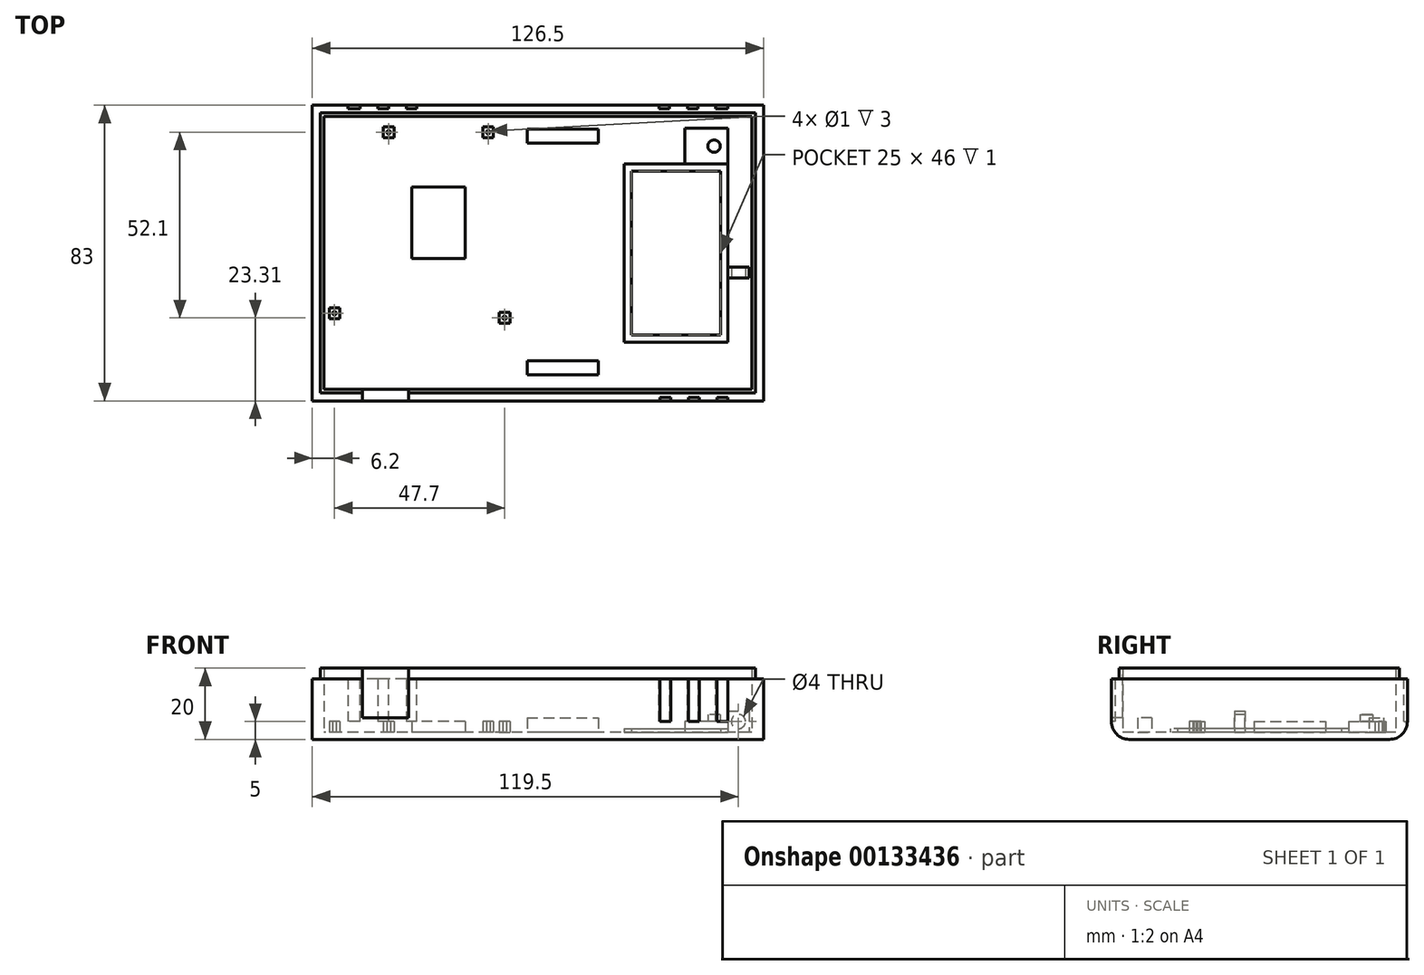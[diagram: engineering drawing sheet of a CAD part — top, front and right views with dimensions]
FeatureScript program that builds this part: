
annotation { "Feature Type Name" : "Feature", "Feature Type Description" : "" }
export const myFeature = defineFeature(function(context is Context, id is Id, definition is map)
    precondition{}
    {
        {
            var Q0;
            Q0=qCreatedBy(makeId("Top.planeOp"),FACE);
            var sketch = newSketch(context, id + "F0", { "sketchPlane" : qUnion([Q0])});
            skLineSegment(sketch, "E0.bottom", {"start": v(63.25, 41.5) * mm, "end": v(-63.25, 41.5) * mm});
            skLineSegment(sketch, "E0.top", {"start": v(63.25, -41.5) * mm, "end": v(-63.25, -41.5) * mm});
            skLineSegment(sketch, "E0.left", {"start": v(63.25, 41.5) * mm, "end": v(63.25, -41.5) * mm});
            skLineSegment(sketch, "E0.right", {"start": v(-63.25, 41.5) * mm, "end": v(-63.25, -41.5) * mm});
            skPoint(sketch, "E0.middle", {"position": v(0, 0) * mm});
            skLineSegment(sketch, "E1.0", {"start": v(-61.25, 39.5) * mm, "end": v(-61.25, -39.5) * mm});
            skLineSegment(sketch, "E1.1", {"start": v(61.25, 39.5) * mm, "end": v(-61.25, 39.5) * mm});
            skLineSegment(sketch, "E1.2", {"start": v(61.25, 39.5) * mm, "end": v(61.25, -39.5) * mm});
            skLineSegment(sketch, "E1.3", {"start": v(61.25, -39.5) * mm, "end": v(-61.25, -39.5) * mm});
            skLineSegment(sketch, "E2", {"start": v(26.25, 23) * mm, "end": v(26.25, -23) * mm});
            skLineSegment(sketch, "E3", {"start": v(26.25, -23) * mm, "end": v(49.25, -23) * mm});
            skLineSegment(sketch, "E4", {"start": v(63.25, 41.5) * mm, "end": v(11.25, 41.5) * mm});
            skLineSegment(sketch, "E5", {"start": v(11.25, 0) * mm, "end": v(-13.75, 0) * mm});
            skLineSegment(sketch, "E6.0", {"start": v(24.25, -25) * mm, "end": v(51.25, -25) * mm});
            skLineSegment(sketch, "E6.1", {"start": v(24.25, 25) * mm, "end": v(24.25, -25) * mm});
            skLineSegment(sketch, "E6.4", {"start": v(51.25, 25) * mm, "end": v(24.25, 25) * mm});
            skLineSegment(sketch, "E7.0", {"start": v(61.05, 39.3) * mm, "end": v(-61.05, 39.3) * mm});
            skLineSegment(sketch, "E7.1", {"start": v(61.05, 39.3) * mm, "end": v(61.05, -39.3) * mm});
            skLineSegment(sketch, "E7.2", {"start": v(61.05, -39.3) * mm, "end": v(-61.05, -39.3) * mm});
            skLineSegment(sketch, "E7.3", {"start": v(-61.05, 39.3) * mm, "end": v(-61.05, -39.3) * mm});
            skLineSegment(sketch, "E8.0", {"start": v(60.05, 38.3) * mm, "end": v(-60.05, 38.3) * mm});
            skLineSegment(sketch, "E8.1", {"start": v(60.05, 38.3) * mm, "end": v(60.05, -38.3) * mm});
            skLineSegment(sketch, "E8.2", {"start": v(60.05, -38.3) * mm, "end": v(-60.05, -38.3) * mm});
            skLineSegment(sketch, "E8.3", {"start": v(-60.05, 38.3) * mm, "end": v(-60.05, -38.3) * mm});
            skLineSegment(sketch, "E9", {"start": v(-63.25, -41.5) * mm, "end": v(-56.25, -41.5) * mm});
            skLineSegment(sketch, "E10", {"start": v(-63.25, -41.5) * mm, "end": v(-43.25, -41.5) * mm});
            skLineSegment(sketch, "E11", {"start": v(-43.25, -41.5) * mm, "end": v(-43.25, -38.3) * mm});
            skLineSegment(sketch, "E12", {"start": v(-56.25, -41.5) * mm, "end": v(-56.25, -38.3) * mm});
            skLineSegment(sketch, "E13", {"start": v(-61.05, -39.3) * mm, "end": v(-2.75, -39.3) * mm});
            skLineSegment(sketch, "E14.right", {"start": v(-4.75, -14.19) * mm, "end": v(-4.75, -18.2) * mm});
            skPoint(sketch, "E14.middle", {"position": v(-4.37, -16.2) * mm});
            skLineSegment(sketch, "E15", {"start": v(-51.75, 34.8) * mm, "end": v(-55.75, 34.8) * mm});
            skLineSegment(sketch, "E16", {"start": v(-3, 34.8) * mm, "end": v(17, 34.8) * mm});
            skLineSegment(sketch, "E17", {"start": v(17, -34.2) * mm, "end": v(-3, -34.2) * mm});
            skLineSegment(sketch, "E18.1", {"start": v(1, 30.8) * mm, "end": v(15, 30.8) * mm});
            skLineSegment(sketch, "E18.2", {"start": v(15, -30.2) * mm, "end": v(1, -30.2) * mm});
            skLineSegment(sketch, "E18.3", {"start": v(1, -18.2) * mm, "end": v(1, -30.2) * mm});
            skLineSegment(sketch, "E19", {"start": v(15, 30.8) * mm, "end": v(17, 30.8) * mm});
            skLineSegment(sketch, "E20", {"start": v(15, -30.2) * mm, "end": v(17, -30.2) * mm});
            skLineSegment(sketch, "E21", {"start": v(17, -34.2) * mm, "end": v(17, -30.2) * mm});
            skLineSegment(sketch, "E22", {"start": v(17, 30.8) * mm, "end": v(17, 34.8) * mm});
            skLineSegment(sketch, "E23", {"start": v(24.25, 25) * mm, "end": v(36.25, 25) * mm});
            skLineSegment(sketch, "E24", {"start": v(53.25, 25) * mm, "end": v(53.25, 35) * mm});
            skLineSegment(sketch, "E25", {"start": v(53.25, 35) * mm, "end": v(41.25, 35) * mm});
            skLineSegment(sketch, "E26", {"start": v(41.25, 35) * mm, "end": v(41.25, 25) * mm});
            skLineSegment(sketch, "E27", {"start": v(53.25, 30) * mm, "end": v(49.42, 30) * mm});
            skPoint(sketch, "E27.endSnap0", {"position": v(36.25, 30) * mm});
            skCircle(sketch, "E28", {"center": v(49.42, 30) * mm, "radius": 1.75 * mm});
            skLineSegment(sketch, "E29", {"start": v(-60.05, -18.2) * mm, "end": v(-57.05, -18.2) * mm});
            skLineSegment(sketch, "E30", {"start": v(-57.05, -18.2) * mm, "end": v(-57.05, -16.9) * mm});
            skLineSegment(sketch, "E31.bottom", {"start": v(-55.55, -18.4) * mm, "end": v(-58.55, -18.4) * mm});
            skLineSegment(sketch, "E31.top", {"start": v(-55.55, -15.4) * mm, "end": v(-58.55, -15.4) * mm});
            skLineSegment(sketch, "E31.left", {"start": v(-55.55, -18.4) * mm, "end": v(-55.55, -15.4) * mm});
            skLineSegment(sketch, "E31.right", {"start": v(-58.55, -18.4) * mm, "end": v(-58.55, -15.4) * mm});
            skPoint(sketch, "E31.middle", {"position": v(-57.05, -16.9) * mm});
            skPoint(sketch, "E32.middle", {"position": v(-4.75, -18.2) * mm});
            skCircle(sketch, "E33", {"center": v(-57.05, -16.9) * mm, "radius": 0.5 * mm});
            skLineSegment(sketch, "E34", {"start": v(-57.05, -16.9) * mm, "end": v(-57.05, 33.9) * mm});
            skLineSegment(sketch, "E35", {"start": v(-57.05, 33.9) * mm, "end": v(-41.85, 33.9) * mm});
            skLineSegment(sketch, "E36", {"start": v(-41.85, 33.9) * mm, "end": v(-13.95, 33.9) * mm});
            skLineSegment(sketch, "E37.bottom", {"start": v(-40.35, 32.4) * mm, "end": v(-43.35, 32.4) * mm});
            skLineSegment(sketch, "E37.top", {"start": v(-40.35, 35.4) * mm, "end": v(-43.35, 35.4) * mm});
            skLineSegment(sketch, "E37.left", {"start": v(-40.35, 32.4) * mm, "end": v(-40.35, 35.4) * mm});
            skLineSegment(sketch, "E37.right", {"start": v(-43.35, 32.4) * mm, "end": v(-43.35, 35.4) * mm});
            skPoint(sketch, "E37.middle", {"position": v(-41.85, 33.9) * mm});
            skLineSegment(sketch, "E38.bottom", {"start": v(-12.45, 32.41) * mm, "end": v(-15.45, 32.41) * mm});
            skLineSegment(sketch, "E38.top", {"start": v(-12.45, 35.41) * mm, "end": v(-15.45, 35.41) * mm});
            skLineSegment(sketch, "E38.left", {"start": v(-12.45, 32.41) * mm, "end": v(-12.45, 35.41) * mm});
            skLineSegment(sketch, "E38.right", {"start": v(-15.45, 32.41) * mm, "end": v(-15.45, 35.41) * mm});
            skPoint(sketch, "E38.middle", {"position": v(-13.95, 33.91) * mm});
            skCircle(sketch, "E39", {"center": v(-41.85, 33.9) * mm, "radius": 0.5 * mm});
            skCircle(sketch, "E40", {"center": v(-13.95, 33.91) * mm, "radius": 0.5 * mm});
            skLineSegment(sketch, "E41", {"start": v(-41.85, 33.9) * mm, "end": v(-27.9, 33.9) * mm});
            skLineSegment(sketch, "E42", {"start": v(-27.9, 33.9) * mm, "end": v(-27.9, -16.9) * mm});
            skLineSegment(sketch, "E43.bottom", {"start": v(-20.4, -1.5) * mm, "end": v(-35.4, -1.5) * mm});
            skLineSegment(sketch, "E43.top", {"start": v(-20.4, 18.5) * mm, "end": v(-35.4, 18.5) * mm});
            skLineSegment(sketch, "E43.left", {"start": v(-20.4, -1.5) * mm, "end": v(-20.4, 18.5) * mm});
            skLineSegment(sketch, "E43.right", {"start": v(-35.4, -1.5) * mm, "end": v(-35.4, 18.5) * mm});
            skPoint(sketch, "E43.middle", {"position": v(-27.9, 8.5) * mm});
            skLineSegment(sketch, "E44", {"start": v(-3, 0) * mm, "end": v(0, 0) * mm});
            skLineSegment(sketch, "E45", {"start": v(0, 0) * mm, "end": v(-3, 0) * mm});
            skLineSegment(sketch, "E46.0", {"start": v(59.25, -4) * mm, "end": v(59.25, -7) * mm});
            skLineSegment(sketch, "E47", {"start": v(57.25, -7) * mm, "end": v(59.25, -7) * mm});
            skLineSegment(sketch, "E48", {"start": v(57.25, -4) * mm, "end": v(59.25, -4) * mm});
            skLineSegment(sketch, "E49", {"start": v(53.25, -7) * mm, "end": v(53.25, -4) * mm});
            skLineSegment(sketch, "E50", {"start": v(53.25, -7) * mm, "end": v(57.25, -7) * mm});
            skLineSegment(sketch, "E51", {"start": v(53.25, -4) * mm, "end": v(57.25, -4) * mm});
            skLineSegment(sketch, "E52", {"start": v(49.25, -23) * mm, "end": v(51.25, -23) * mm});
            skLineSegment(sketch, "E53", {"start": v(51.25, -23) * mm, "end": v(51.25, 23) * mm});
            skLineSegment(sketch, "E54", {"start": v(51.25, -25) * mm, "end": v(53.25, -25) * mm});
            skLineSegment(sketch, "E55", {"start": v(51.25, 25) * mm, "end": v(53.25, 25) * mm});
            skLineSegment(sketch, "E56", {"start": v(53.25, 25) * mm, "end": v(53.25, -25) * mm});
            skLineSegment(sketch, "E57", {"start": v(26.25, 23) * mm, "end": v(51.25, 23) * mm});
            skLineSegment(sketch, "E58", {"start": v(-4.75, -18.2) * mm, "end": v(-4.75, 35.4) * mm});
            skLineSegment(sketch, "E59.bottom", {"start": v(-7.85, -16.7) * mm, "end": v(-10.85, -16.7) * mm});
            skLineSegment(sketch, "E59.top", {"start": v(-7.85, -19.69) * mm, "end": v(-10.85, -19.69) * mm});
            skLineSegment(sketch, "E59.left", {"start": v(-7.85, -16.7) * mm, "end": v(-7.85, -19.69) * mm});
            skLineSegment(sketch, "E59.right", {"start": v(-10.85, -16.7) * mm, "end": v(-10.85, -19.69) * mm});
            skPoint(sketch, "E59.middle", {"position": v(-9.35, -18.19) * mm});
            skCircle(sketch, "E60", {"center": v(-9.35, -18.19) * mm, "radius": 0.5 * mm});
            skLineSegment(sketch, "E61", {"start": v(36.25, 25) * mm, "end": v(24.25, 25) * mm});
            skLineSegment(sketch, "E62", {"start": v(1, 30.8) * mm, "end": v(-3, 30.8) * mm});
            skLineSegment(sketch, "E63", {"start": v(1, -30.2) * mm, "end": v(-3, -30.2) * mm});
            skLineSegment(sketch, "E64", {"start": v(-3, 30.8) * mm, "end": v(-3, 34.8) * mm});
            skLineSegment(sketch, "E65", {"start": v(-3, -30.2) * mm, "end": v(-3, -34.2) * mm});
            skLineSegment(sketch, "E66", {"start": v(-3, -34.2) * mm, "end": v(-3, -30.2) * mm});
            skLineSegment(sketch, "E67", {"start": v(-3, -30.2) * mm, "end": v(17, -30.2) * mm});
            skSolve(sketch);
        }
        {
            var Q0;
            {var subQ8=sQuery(id+"F0.wireOp",EDGE,"E0.bottom");Q0=makeQuery(id+"F0.imprint","IMPRINT",FACE,{"disambiguationData":[TD([[makeQuery(id+"F0.imprint","IMPRINT",EDGE,{"derivedFrom":subQ8}),1.0]])]});}
            var Q1;
            {var subQ4=sQuery(id+"F0.wireOp",EDGE,"E4");Q1=makeQuery(id+"F0.imprint","IMPRINT",FACE,{"disambiguationData":[TD([[makeQuery(id+"F0.imprint","IMPRINT",EDGE,{"derivedFrom":subQ4}),1.0]])]});}
            var Q2;
            Q2=makeQuery(id+"F0.imprint","IMPRINT",FACE,{"disambiguationData":[TD([[makeQuery(id+"F0.imprint","IMPRINT",EDGE,{"derivedFrom":sQuery(id+"F0.wireOp",EDGE,"E1.0")}),1.0]])]});
            var Q3;
            {var subQ8=sQuery(id+"F0.wireOp",EDGE,"E0.top");Q3=makeQuery(id+"F0.imprint","IMPRINT",FACE,{"disambiguationData":[TD([[makeQuery(id+"F0.imprint","IMPRINT",EDGE,{"derivedFrom":subQ8}),-1.0]])]});}
            var Q4;
            {var subQ5=sQuery(id+"F0.wireOp",EDGE,"E1.3");var subQ6=sQuery(id+"F0.wireOp",EDGE,"E1.2");var subQ7=makeQuery(id+"F0.imprint","INTERSECT",VERTEX,{"derivedFrom":[subQ6,subQ5]});Q4=makeQuery(id+"F0.imprint","IMPRINT",FACE,{"disambiguationData":[TD([[makeQuery(id+"F0.imprint","IMPRINT",EDGE,{"disambiguationData":[TD([[subQ7,1.0]])],"derivedFrom":subQ6}),-1.0]])]});}
            var Q5;
            {var subQ0=sQuery(id+"F0.wireOp",EDGE,"E11");var subQ1=sQuery(id+"F0.wireOp",EDGE,"E1.3");var subQ2=makeQuery(id+"F0.imprint","INTERSECT",VERTEX,{"derivedFrom":[subQ1,subQ0]});Q5=makeQuery(id+"F0.imprint","IMPRINT",FACE,{"disambiguationData":[TD([[makeQuery(id+"F0.imprint","IMPRINT",EDGE,{"disambiguationData":[TD([[subQ2,-1.0]])],"derivedFrom":subQ1}),-1.0]])]});}
            var Q6;
            {var subQ0=sQuery(id+"F0.wireOp",EDGE,"E11");var subQ1=sQuery(id+"F0.wireOp",EDGE,"E1.3");var subQ2=makeQuery(id+"F0.imprint","INTERSECT",VERTEX,{"derivedFrom":[subQ1,subQ0]});Q6=makeQuery(id+"F0.imprint","IMPRINT",FACE,{"disambiguationData":[TD([[makeQuery(id+"F0.imprint","IMPRINT",EDGE,{"disambiguationData":[TD([[subQ2,-1.0]])],"derivedFrom":subQ1}),1.0]])]});}
            extrude(context, id + "F1", {"entities" : qUnion([Q0, Q1, Q2, Q3, Q4, Q5, Q6]), "depth" : 17 * mm});
        }
        {
            var Q0;
            Q0=makeQuery(id+"F0.imprint","IMPRINT",FACE,{"disambiguationData":[TD([[makeQuery(id+"F0.imprint","IMPRINT",EDGE,{"derivedFrom":sQuery(id+"F0.wireOp",EDGE,"E6.0")}),-1.0]])]});
            var Q1;
            {var subQ3=sQuery(id+"F0.wireOp",EDGE,"E7.0");Q1=makeQuery(id+"F0.imprint","IMPRINT",FACE,{"disambiguationData":[TD([[makeQuery(id+"F0.imprint","IMPRINT",EDGE,{"derivedFrom":subQ3}),1.0]])]});}
            var Q2;
            Q2=makeQuery(id+"F0.imprint","IMPRINT",FACE,{"disambiguationData":[TD([[makeQuery(id+"F0.imprint","IMPRINT",EDGE,{"derivedFrom":sQuery(id+"F0.wireOp",EDGE,"JjJUV9Ur-tdpk-wXrh-GGUp-oHRZlqTkyCgY")}),1.0]])]});
            var Q3;
            {var subQ0=sQuery(id+"F0.wireOp",EDGE,"QEQ184YT-IDw3-G2xn-FZOk-iXz4uPS1LeEL");Q3=makeQuery(id+"F0.imprint","IMPRINT",FACE,{"disambiguationData":[TD([[makeQuery(id+"F0.imprint","IMPRINT",EDGE,{"derivedFrom":subQ0}),1.0]])]});}
            var Q4;
            {var subQ0=sQuery(id+"F0.wireOp",EDGE,"E11");var subQ1=sQuery(id+"F0.wireOp",EDGE,"E7.2");var subQ2=makeQuery(id+"F0.imprint","INTERSECT",VERTEX,{"derivedFrom":[subQ1,subQ0]});Q4=makeQuery(id+"F0.imprint","IMPRINT",FACE,{"disambiguationData":[TD([[makeQuery(id+"F0.imprint","IMPRINT",EDGE,{"disambiguationData":[TD([[subQ2,-1.0]])],"derivedFrom":subQ1}),-1.0]])]});}
            var Q5;
            {var subQ0=sQuery(id+"F0.wireOp",EDGE,"E11");var subQ1=sQuery(id+"F0.wireOp",EDGE,"E1.3");var subQ2=makeQuery(id+"F0.imprint","INTERSECT",VERTEX,{"derivedFrom":[subQ1,subQ0]});Q5=makeQuery(id+"F0.imprint","IMPRINT",FACE,{"disambiguationData":[TD([[makeQuery(id+"F0.imprint","IMPRINT",EDGE,{"disambiguationData":[TD([[subQ2,-1.0]])],"derivedFrom":subQ1}),-1.0]])]});}
            var Q6;
            {var subQ0=sQuery(id+"F0.wireOp",EDGE,"E11");var subQ1=sQuery(id+"F0.wireOp",EDGE,"E1.3");var subQ2=makeQuery(id+"F0.imprint","INTERSECT",VERTEX,{"derivedFrom":[subQ1,subQ0]});Q6=makeQuery(id+"F0.imprint","IMPRINT",FACE,{"disambiguationData":[TD([[makeQuery(id+"F0.imprint","IMPRINT",EDGE,{"disambiguationData":[TD([[subQ2,-1.0]])],"derivedFrom":subQ1}),1.0]])]});}
            var Q7;
            {var subQ5=sQuery(id+"F0.wireOp",EDGE,"qdQUFwnO-mMan-IZQE-LNTO-aOdIMTajD8fE");Q7=makeQuery(id+"F0.imprint","IMPRINT",FACE,{"disambiguationData":[TD([[makeQuery(id+"F0.imprint","IMPRINT",EDGE,{"derivedFrom":subQ5}),1.0]])]});}
            var Q8;
            Q8=makeQuery(id+"F0.imprint","IMPRINT",FACE,{"disambiguationData":[TD([[makeQuery(id+"F0.imprint","IMPRINT",EDGE,{"derivedFrom":sQuery(id+"F0.wireOp",EDGE,"Yb7JVAUj-9wBk-Ivu1-Xwfn-bJDCMV5gfvpt.right")}),-1.0]])]});
            var Q9;
            {var subQ1=sQuery(id+"F0.wireOp",EDGE,"E14.left");Q9=makeQuery(id+"F0.imprint","IMPRINT",FACE,{"disambiguationData":[TD([[makeQuery(id+"F0.imprint","IMPRINT",EDGE,{"derivedFrom":subQ1}),1.0]])]});}
            var Q10;
            {var subQ4=sQuery(id+"F0.wireOp",EDGE,"E14.bottom");Q10=makeQuery(id+"F0.imprint","IMPRINT",FACE,{"disambiguationData":[TD([[makeQuery(id+"F0.imprint","IMPRINT",EDGE,{"derivedFrom":subQ4}),1.0]])]});}
            var Q11;
            {var subQ3=sQuery(id+"F0.wireOp",EDGE,"Yb7JVAUj-9wBk-Ivu1-Xwfn-bJDCMV5gfvpt.bottom");Q11=makeQuery(id+"F0.imprint","IMPRINT",FACE,{"disambiguationData":[TD([[makeQuery(id+"F0.imprint","IMPRINT",EDGE,{"derivedFrom":subQ3}),1.0]])]});}
            var Q12;
            {var subQ0=sQuery(id+"F0.wireOp",EDGE,"dg6y9XsB-MLs8-b2t9-6rjp-xuShEImU9hPs");var subQ1=sQuery(id+"F0.wireOp",EDGE,"4MlRj56P-oCF8-BNxh-Kgjj-tpuhawxrlBJX");var subQ2=makeQuery(id+"F0.imprint","INTERSECT",VERTEX,{"derivedFrom":[subQ1,subQ0]});Q12=makeQuery(id+"F0.imprint","IMPRINT",FACE,{"disambiguationData":[TD([[makeQuery(id+"F0.imprint","IMPRINT",EDGE,{"disambiguationData":[TD([[subQ2,1.0]])],"derivedFrom":subQ1}),1.0]])]});}
            var Q13;
            {var subQ1=sQuery(id+"F0.wireOp",EDGE,"Yb7JVAUj-9wBk-Ivu1-Xwfn-bJDCMV5gfvpt.top");Q13=makeQuery(id+"F0.imprint","IMPRINT",FACE,{"disambiguationData":[TD([[makeQuery(id+"F0.imprint","IMPRINT",EDGE,{"derivedFrom":subQ1}),1.0]])]});}
            var Q14;
            {var subQ5=sQuery(id+"F0.wireOp",EDGE,"2K8RhCZ3-myJd-tRPz-d2vV-Ilw3Z1lNlUKb");Q14=makeQuery(id+"F0.imprint","IMPRINT",FACE,{"disambiguationData":[TD([[makeQuery(id+"F0.imprint","IMPRINT",EDGE,{"derivedFrom":subQ5}),1.0]])]});}
            var Q15;
            {var subQ0=sQuery(id+"F0.wireOp",EDGE,"E11");var subQ5=sQuery(id+"F0.wireOp",EDGE,"E13");var subQ7=makeQuery(id+"F0.imprint","INTERSECT",VERTEX,{"derivedFrom":[subQ0,subQ5]});Q15=makeQuery(id+"F0.imprint","IMPRINT",FACE,{"disambiguationData":[TD([[makeQuery(id+"F0.imprint","IMPRINT",EDGE,{"disambiguationData":[TD([[subQ7,1.0]])],"derivedFrom":subQ5}),1.0]])]});}
            var Q16;
            Q16=makeQuery(id+"F0.imprint","IMPRINT",FACE,{"disambiguationData":[TD([[makeQuery(id+"F0.imprint","IMPRINT",EDGE,{"derivedFrom":sQuery(id+"F0.wireOp",EDGE,"FxGr0PKn-y8hg-s7OV-rVK9-zofutq62NFjj")}),-1.0]])]});
            var Q17;
            Q17=makeQuery(id+"F0.imprint","IMPRINT",FACE,{"disambiguationData":[TD([[makeQuery(id+"F0.imprint","IMPRINT",EDGE,{"derivedFrom":sQuery(id+"F0.wireOp",EDGE,"M7WSyIMN-nxIa-V6t1-Xdwt-x6DTuTfdMUkq")}),1.0]])]});
            var Q18;
            Q18=makeQuery(id+"F0.imprint","IMPRINT",FACE,{"disambiguationData":[TD([[makeQuery(id+"F0.imprint","IMPRINT",EDGE,{"derivedFrom":sQuery(id+"F0.wireOp",EDGE,"RjNV0yv9-Uhwm-tNHm-vLTt-bpPdpbskBz0X")}),1.0]])]});
            var Q19;
            {var subQ0=sQuery(id+"F0.wireOp",EDGE,"MmGPWXn9-bgj3-SnPU-f73x-K2FSZj5xh2pY");Q19=makeQuery(id+"F0.imprint","IMPRINT",FACE,{"disambiguationData":[TD([[makeQuery(id+"F0.imprint","IMPRINT",EDGE,{"derivedFrom":subQ0}),-1.0]])]});}
            var Q20;
            {var subQ0=sQuery(id+"F0.wireOp",EDGE,"ythX9w36-mhEy-aItk-m4XK-AgucC76ztnV9");Q20=makeQuery(id+"F0.imprint","IMPRINT",FACE,{"disambiguationData":[TD([[makeQuery(id+"F0.imprint","IMPRINT",EDGE,{"derivedFrom":subQ0}),1.0]])]});}
            var Q21;
            {var subQ1=sQuery(id+"F0.wireOp",EDGE,"E16");Q21=makeQuery(id+"F0.imprint","IMPRINT",FACE,{"disambiguationData":[TD([[makeQuery(id+"F0.imprint","IMPRINT",EDGE,{"derivedFrom":subQ1}),-1.0]])]});}
            var Q22;
            {var subQ3=sQuery(id+"F0.wireOp",EDGE,"E23");Q22=makeQuery(id+"F0.imprint","IMPRINT",FACE,{"disambiguationData":[TD([[makeQuery(id+"F0.imprint","IMPRINT",EDGE,{"derivedFrom":subQ3}),1.0]])]});}
            var Q23;
            Q23=makeQuery(id+"F0.imprint","IMPRINT",FACE,{"disambiguationData":[TD([[makeQuery(id+"F0.imprint","IMPRINT",EDGE,{"derivedFrom":sQuery(id+"F0.wireOp",EDGE,"E28")}),1.0]])]});
            var Q24;
            Q24=makeQuery(id+"F0.imprint","IMPRINT",FACE,{"disambiguationData":[TD([[makeQuery(id+"F0.imprint","IMPRINT",EDGE,{"derivedFrom":sQuery(id+"F0.wireOp",EDGE,"Upk9CpIW-mo80-YB5J-z0Jw-Bhem0cwXyb0w")}),1.0]])]});
            var Q25;
            {var subQ0=sQuery(id+"F0.wireOp",EDGE,"E34");var subQ1=sQuery(id+"F0.wireOp",EDGE,"E30");var subQ2=makeQuery(id+"F0.imprint","INTERSECT",VERTEX,{"derivedFrom":[subQ1,subQ0]});Q25=makeQuery(id+"F0.imprint","IMPRINT",FACE,{"disambiguationData":[TD([[makeQuery(id+"F0.imprint","IMPRINT",EDGE,{"disambiguationData":[TD([[subQ2,1.0]])],"derivedFrom":subQ1}),1.0]])]});}
            var Q26;
            {var subQ0=sQuery(id+"F0.wireOp",EDGE,"E34");var subQ1=sQuery(id+"F0.wireOp",EDGE,"E30");var subQ2=makeQuery(id+"F0.imprint","INTERSECT",VERTEX,{"derivedFrom":[subQ1,subQ0]});Q26=makeQuery(id+"F0.imprint","IMPRINT",FACE,{"disambiguationData":[TD([[makeQuery(id+"F0.imprint","IMPRINT",EDGE,{"disambiguationData":[TD([[subQ2,1.0]])],"derivedFrom":subQ1}),-1.0]])]});}
            var Q27;
            Q27=makeQuery(id+"F0.imprint","IMPRINT",FACE,{"disambiguationData":[TD([[makeQuery(id+"F0.imprint","IMPRINT",EDGE,{"derivedFrom":sQuery(id+"F0.wireOp",EDGE,"E40")}),1.0]])]});
            var Q28;
            {var subQ0=sQuery(id+"F0.wireOp",EDGE,"E41");var subQ1=sQuery(id+"F0.wireOp",EDGE,"E35");var subQ2=makeQuery(id+"F0.imprint","INTERSECT",VERTEX,{"derivedFrom":[subQ1,subQ0]});Q28=makeQuery(id+"F0.imprint","IMPRINT",FACE,{"disambiguationData":[TD([[makeQuery(id+"F0.imprint","IMPRINT",EDGE,{"disambiguationData":[TD([[subQ2,1.0]])],"derivedFrom":subQ1}),1.0]])]});}
            var Q29;
            {var subQ0=sQuery(id+"F0.wireOp",EDGE,"E41");var subQ1=sQuery(id+"F0.wireOp",EDGE,"E35");var subQ2=makeQuery(id+"F0.imprint","INTERSECT",VERTEX,{"derivedFrom":[subQ1,subQ0]});Q29=makeQuery(id+"F0.imprint","IMPRINT",FACE,{"disambiguationData":[TD([[makeQuery(id+"F0.imprint","IMPRINT",EDGE,{"disambiguationData":[TD([[subQ2,1.0]])],"derivedFrom":subQ1}),-1.0]])]});}
            var Q30;
            Q30=makeQuery(id+"F0.imprint","IMPRINT",FACE,{"disambiguationData":[TD([[makeQuery(id+"F0.imprint","IMPRINT",EDGE,{"derivedFrom":sQuery(id+"F0.wireOp",EDGE,"E2")}),1.0]])]});
            var Q31;
            Q31=makeQuery(id+"F0.imprint","IMPRINT",FACE,{"disambiguationData":[TD([[makeQuery(id+"F0.imprint","IMPRINT",EDGE,{"derivedFrom":sQuery(id+"F0.wireOp",EDGE,"E46.0")}),-1.0]])]});
            var Q32;
            Q32=makeQuery(id+"F0.imprint","IMPRINT",FACE,{"disambiguationData":[TD([[makeQuery(id+"F0.imprint","IMPRINT",EDGE,{"derivedFrom":sQuery(id+"F0.wireOp",EDGE,"E60")}),1.0]])]});
            var Q33;
            {var subQ3=sQuery(id+"F0.wireOp",EDGE,"E59.bottom");Q33=makeQuery(id+"F0.imprint","IMPRINT",FACE,{"disambiguationData":[TD([[makeQuery(id+"F0.imprint","IMPRINT",EDGE,{"derivedFrom":subQ3}),1.0]])]});}
            var Q34;
            {var subQ0=sQuery(id+"F0.wireOp",EDGE,"E25");Q34=makeQuery(id+"F0.imprint","IMPRINT",FACE,{"disambiguationData":[TD([[makeQuery(id+"F0.imprint","IMPRINT",EDGE,{"derivedFrom":subQ0}),1.0]])]});}
            extrude(context, id + "F2", {"entities" : qUnion([Q0, Q1, Q2, Q3, Q4, Q5, Q6, Q7, Q8, Q9, Q10, Q11, Q12, Q13, Q14, Q15, Q16, Q17, Q18, Q19, Q20, Q21, Q22, Q23, Q24, Q25, Q26, Q27, Q28, Q29, Q30, Q31, Q32, Q33, Q34]), "operationType" : NewBodyOperationType.ADD, "depth" : 2 * mm});
        }
        {
            var Q0;
            Q0=makeQuery(id+"F1.opExtrude","CAP_EDGE",EDGE,{"disambiguationData":[OSD([sQuery(id+"F0.wireOp",EDGE,"E0.bottom"),sQuery(id+"F0.wireOp",EDGE,"E4")])],"isStart":true});
            var Q1;
            Q1=makeQuery(id+"F1.opExtrude","CAP_EDGE",EDGE,{"disambiguationData":[OSD([sQuery(id+"F0.wireOp",EDGE,"E0.top")])],"isStart":true});
            fillet(context, id + "F3", {"entities" : qUnion([Q0, Q1]), "radius" : 5 * mm, "tangentPropagation" : true, "allowEdgeOverflow" : false});
        }
        {
            var Q0;
            Q0=makeQuery(id+"F1.opExtrude","SWEPT_FACE",FACE,{"disambiguationData":[OSD([sQuery(id+"F0.wireOp",EDGE,"E0.bottom"),sQuery(id+"F0.wireOp",EDGE,"E4")])]});
            var sketch = newSketch(context, id + "F4", { "sketchPlane" : qUnion([Q0])});
            skLineSegment(sketch, "E68", {"start": v(-63.25, 17) * mm, "end": v(-0.25, 17) * mm});
            skLineSegment(sketch, "E69", {"start": v(-0.25, 17) * mm, "end": v(-0.25, 3) * mm});
            skLineSegment(sketch, "E70", {"start": v(-63.25, 17) * mm, "end": v(-53.25, 17) * mm});
            skLineSegment(sketch, "E71", {"start": v(-53.25, 17) * mm, "end": v(-53.25, 5) * mm});
            skLineSegment(sketch, "E72", {"start": v(-53.25, 5) * mm, "end": v(-49.9, 5) * mm});
            skLineSegment(sketch, "E73", {"start": v(-49.9, 5) * mm, "end": v(-49.9, 17) * mm});
            skLineSegment(sketch, "E74", {"start": v(-49.9, 17) * mm, "end": v(-44.9, 17) * mm});
            skLineSegment(sketch, "E75", {"start": v(-44.9, 17) * mm, "end": v(-44.9, 5) * mm});
            skLineSegment(sketch, "E76", {"start": v(-44.9, 5) * mm, "end": v(-41.9, 5) * mm});
            skLineSegment(sketch, "E77", {"start": v(-41.9, 5) * mm, "end": v(-41.9, 17) * mm});
            skLineSegment(sketch, "E78", {"start": v(-41.9, 17) * mm, "end": v(-36.9, 17) * mm});
            skLineSegment(sketch, "E79", {"start": v(-36.9, 17) * mm, "end": v(-36.9, 5) * mm});
            skLineSegment(sketch, "E80", {"start": v(-36.9, 5) * mm, "end": v(-33.9, 5) * mm});
            skLineSegment(sketch, "E81", {"start": v(-33.9, 5) * mm, "end": v(-33.9, 17) * mm});
            skLineSegment(sketch, "E82.MirrorCS", {"start": v(33.9, 5) * mm, "end": v(33.9, 17) * mm});
            skLineSegment(sketch, "E83.MirrorCS", {"start": v(36.9, 17) * mm, "end": v(36.9, 5) * mm});
            skLineSegment(sketch, "E84.MirrorCS", {"start": v(41.9, 5) * mm, "end": v(41.9, 17) * mm});
            skLineSegment(sketch, "E85.MirrorCS", {"start": v(44.9, 17) * mm, "end": v(44.9, 5) * mm});
            skLineSegment(sketch, "E86.MirrorCS", {"start": v(49.9, 5) * mm, "end": v(49.9, 17) * mm});
            skLineSegment(sketch, "E87.MirrorCS", {"start": v(53.25, 17) * mm, "end": v(53.25, 5) * mm});
            skLineSegment(sketch, "E88.MirrorCS", {"start": v(36.9, 5) * mm, "end": v(33.9, 5) * mm});
            skLineSegment(sketch, "E89.MirrorCS", {"start": v(44.9, 5) * mm, "end": v(41.9, 5) * mm});
            skLineSegment(sketch, "E90.MirrorCS", {"start": v(63.25, 17) * mm, "end": v(0.25, 17) * mm});
            skLineSegment(sketch, "E91.MirrorCS", {"start": v(53.25, 5) * mm, "end": v(49.9, 5) * mm});
            skLineSegment(sketch, "E92", {"start": v(33.9, 17) * mm, "end": v(36.9, 17) * mm});
            skLineSegment(sketch, "E93", {"start": v(41.9, 17) * mm, "end": v(44.9, 17) * mm});
            skLineSegment(sketch, "E94", {"start": v(49.9, 17) * mm, "end": v(53.25, 17) * mm});
            skSolve(sketch);
        }
        {
            var Q0;
            Q0=makeQuery(id+"F0.imprint","IMPRINT",FACE,{"disambiguationData":[TD([[makeQuery(id+"F0.imprint","IMPRINT",EDGE,{"derivedFrom":sQuery(id+"F0.wireOp",EDGE,"JjJUV9Ur-tdpk-wXrh-GGUp-oHRZlqTkyCgY")}),-1.0]])]});
            var Q1;
            Q1=makeQuery(id+"F0.imprint","IMPRINT",FACE,{"disambiguationData":[TD([[makeQuery(id+"F0.imprint","IMPRINT",EDGE,{"derivedFrom":sQuery(id+"F0.wireOp",EDGE,"E2")}),-1.0]])]});
            extrude(context, id + "F5", {"entities" : qUnion([Q0, Q1]), "operationType" : NewBodyOperationType.ADD, "depth" : 3 * mm});
        }
        {
            var Q0;
            {var subQ3=sQuery(id+"F0.wireOp",EDGE,"E7.0");Q0=makeQuery(id+"F0.imprint","IMPRINT",FACE,{"disambiguationData":[TD([[makeQuery(id+"F0.imprint","IMPRINT",EDGE,{"derivedFrom":subQ3}),1.0]])]});}
            var Q1;
            {var subQ0=sQuery(id+"F0.wireOp",EDGE,"E11");var subQ1=sQuery(id+"F0.wireOp",EDGE,"E8.2");var subQ2=makeQuery(id+"F0.imprint","INTERSECT",VERTEX,{"derivedFrom":[subQ1,subQ0]});Q1=makeQuery(id+"F0.imprint","IMPRINT",FACE,{"disambiguationData":[TD([[makeQuery(id+"F0.imprint","IMPRINT",EDGE,{"disambiguationData":[TD([[subQ2,-1.0]])],"derivedFrom":subQ1}),1.0]])]});}
            extrude(context, id + "F6", {"entities" : qUnion([Q0, Q1]), "operationType" : NewBodyOperationType.ADD, "depth" : 20 * mm, "hasSecondDirection" : true, "secondDirectionOppositeDirection" : false, "secondDirectionDepth" : 2 * mm});
        }
        {
            var Q0;
            {var subQ5=sQuery(id+"F0.wireOp",EDGE,"qdQUFwnO-mMan-IZQE-LNTO-aOdIMTajD8fE");Q0=makeQuery(id+"F0.imprint","IMPRINT",FACE,{"disambiguationData":[TD([[makeQuery(id+"F0.imprint","IMPRINT",EDGE,{"derivedFrom":subQ5}),1.0]])]});}
            var Q1;
            {var subQ4=sQuery(id+"F0.wireOp",EDGE,"E14.left");Q1=makeQuery(id+"F0.imprint","IMPRINT",FACE,{"disambiguationData":[TD([[makeQuery(id+"F0.imprint","IMPRINT",EDGE,{"derivedFrom":subQ4}),1.0]])]});}
            var Q2;
            Q2=makeQuery(id+"F0.imprint","IMPRINT",FACE,{"disambiguationData":[TD([[makeQuery(id+"F0.imprint","IMPRINT",EDGE,{"derivedFrom":sQuery(id+"F0.wireOp",EDGE,"Yb7JVAUj-9wBk-Ivu1-Xwfn-bJDCMV5gfvpt.right")}),-1.0]])]});
            var Q3;
            {var subQ3=sQuery(id+"F0.wireOp",EDGE,"Yb7JVAUj-9wBk-Ivu1-Xwfn-bJDCMV5gfvpt.bottom");Q3=makeQuery(id+"F0.imprint","IMPRINT",FACE,{"disambiguationData":[TD([[makeQuery(id+"F0.imprint","IMPRINT",EDGE,{"derivedFrom":subQ3}),1.0]])]});}
            var Q4;
            {var subQ1=sQuery(id+"F0.wireOp",EDGE,"E14.bottom");Q4=makeQuery(id+"F0.imprint","IMPRINT",FACE,{"disambiguationData":[TD([[makeQuery(id+"F0.imprint","IMPRINT",EDGE,{"derivedFrom":subQ1}),1.0]])]});}
            var Q5;
            {var subQ5=sQuery(id+"F0.wireOp",EDGE,"2K8RhCZ3-myJd-tRPz-d2vV-Ilw3Z1lNlUKb");Q5=makeQuery(id+"F0.imprint","IMPRINT",FACE,{"disambiguationData":[TD([[makeQuery(id+"F0.imprint","IMPRINT",EDGE,{"derivedFrom":subQ5}),1.0]])]});}
            var Q6;
            Q6=makeQuery(id+"F0.imprint","IMPRINT",FACE,{"disambiguationData":[TD([[makeQuery(id+"F0.imprint","IMPRINT",EDGE,{"derivedFrom":sQuery(id+"F0.wireOp",EDGE,"FxGr0PKn-y8hg-s7OV-rVK9-zofutq62NFjj")}),-1.0]])]});
            var Q7;
            {var subQ3=sQuery(id+"F0.wireOp",EDGE,"E23");Q7=makeQuery(id+"F0.imprint","IMPRINT",FACE,{"disambiguationData":[TD([[makeQuery(id+"F0.imprint","IMPRINT",EDGE,{"derivedFrom":subQ3}),1.0]])]});}
            var Q8;
            Q8=makeQuery(id+"F0.imprint","IMPRINT",FACE,{"disambiguationData":[TD([[makeQuery(id+"F0.imprint","IMPRINT",EDGE,{"derivedFrom":sQuery(id+"F0.wireOp",EDGE,"E28")}),1.0]])]});
            var Q9;
            {var subQ5=sQuery(id+"F0.wireOp",EDGE,"E43.left");Q9=makeQuery(id+"F0.imprint","IMPRINT",FACE,{"disambiguationData":[TD([[makeQuery(id+"F0.imprint","IMPRINT",EDGE,{"derivedFrom":subQ5}),1.0]])]});}
            var Q10;
            {var subQ5=sQuery(id+"F0.wireOp",EDGE,"E43.right");Q10=makeQuery(id+"F0.imprint","IMPRINT",FACE,{"disambiguationData":[TD([[makeQuery(id+"F0.imprint","IMPRINT",EDGE,{"derivedFrom":subQ5}),-1.0]])]});}
            var Q11;
            {var subQ1=sQuery(id+"F0.wireOp",EDGE,"E38.bottom");Q11=makeQuery(id+"F0.imprint","IMPRINT",FACE,{"disambiguationData":[TD([[makeQuery(id+"F0.imprint","IMPRINT",EDGE,{"derivedFrom":subQ1}),-1.0]])]});}
            var Q12;
            {var subQ1=sQuery(id+"F0.wireOp",EDGE,"E37.top");Q12=makeQuery(id+"F0.imprint","IMPRINT",FACE,{"disambiguationData":[TD([[makeQuery(id+"F0.imprint","IMPRINT",EDGE,{"derivedFrom":subQ1}),1.0]])]});}
            var Q13;
            {var subQ1=sQuery(id+"F0.wireOp",EDGE,"E37.bottom");Q13=makeQuery(id+"F0.imprint","IMPRINT",FACE,{"disambiguationData":[TD([[makeQuery(id+"F0.imprint","IMPRINT",EDGE,{"derivedFrom":subQ1}),-1.0]])]});}
            var Q14;
            Q14=makeQuery(id+"F0.imprint","IMPRINT",FACE,{"disambiguationData":[TD([[makeQuery(id+"F0.imprint","IMPRINT",EDGE,{"derivedFrom":sQuery(id+"F0.wireOp",EDGE,"E32.bottom")}),1.0]])]});
            var Q15;
            {var subQ4=sQuery(id+"F0.wireOp",EDGE,"E31.bottom");Q15=makeQuery(id+"F0.imprint","IMPRINT",FACE,{"disambiguationData":[TD([[makeQuery(id+"F0.imprint","IMPRINT",EDGE,{"derivedFrom":subQ4}),-1.0]])]});}
            var Q16;
            {var subQ3=sQuery(id+"F0.wireOp",EDGE,"E29");var subQ5=sQuery(id+"F0.wireOp",EDGE,"E30");var subQ6=makeQuery(id+"F0.imprint","INTERSECT",VERTEX,{"derivedFrom":[subQ3,subQ5]});Q16=makeQuery(id+"F0.imprint","IMPRINT",FACE,{"disambiguationData":[TD([[makeQuery(id+"F0.imprint","IMPRINT",EDGE,{"disambiguationData":[TD([[subQ6,1.0]])],"derivedFrom":subQ3}),1.0]])]});}
            var Q17;
            {var subQ3=sQuery(id+"F0.wireOp",EDGE,"E59.bottom");Q17=makeQuery(id+"F0.imprint","IMPRINT",FACE,{"disambiguationData":[TD([[makeQuery(id+"F0.imprint","IMPRINT",EDGE,{"derivedFrom":subQ3}),1.0]])]});}
            var Q18;
            {var subQ0=sQuery(id+"F0.wireOp",EDGE,"E25");Q18=makeQuery(id+"F0.imprint","IMPRINT",FACE,{"disambiguationData":[TD([[makeQuery(id+"F0.imprint","IMPRINT",EDGE,{"derivedFrom":subQ0}),1.0]])]});}
            extrude(context, id + "F7", {"entities" : qUnion([Q0, Q1, Q2, Q3, Q4, Q5, Q6, Q7, Q8, Q9, Q10, Q11, Q12, Q13, Q14, Q15, Q16, Q17, Q18]), "operationType" : NewBodyOperationType.ADD, "depth" : 5 * mm});
        }
        {
            var Q0;
            Q0=makeQuery(id+"F1.opExtrude","SWEPT_FACE",FACE,{"disambiguationData":[OSD([sQuery(id+"F0.wireOp",EDGE,"E0.top"),sQuery(id+"F0.wireOp",EDGE,"E10")])]});
            var sketch = newSketch(context, id + "F8", { "sketchPlane" : qUnion([Q0])});
            skLineSegment(sketch, "E95", {"start": v(-63.25, 17) * mm, "end": v(-49.25, 17) * mm});
            skLineSegment(sketch, "E96", {"start": v(-49.25, 17) * mm, "end": v(-49.25, 6) * mm});
            skLineSegment(sketch, "E97", {"start": v(-49.25, 6) * mm, "end": v(-36.25, 6) * mm});
            skLineSegment(sketch, "E98", {"start": v(-36.25, 6) * mm, "end": v(-36.25, 20) * mm});
            skLineSegment(sketch, "E99", {"start": v(-36.25, 20) * mm, "end": v(-49.25, 20) * mm});
            skLineSegment(sketch, "E100", {"start": v(-49.25, 20) * mm, "end": v(-49.25, 17) * mm});
            skLineSegment(sketch, "E101", {"start": v(63.25, 17) * mm, "end": v(53.25, 17) * mm});
            skLineSegment(sketch, "E102", {"start": v(53.25, 17) * mm, "end": v(50.25, 17) * mm});
            skLineSegment(sketch, "E103", {"start": v(50.25, 17) * mm, "end": v(45.25, 17) * mm});
            skLineSegment(sketch, "E104", {"start": v(45.25, 17) * mm, "end": v(42.25, 17) * mm});
            skLineSegment(sketch, "E105", {"start": v(42.25, 17) * mm, "end": v(37.25, 17) * mm});
            skLineSegment(sketch, "E106", {"start": v(37.25, 17) * mm, "end": v(34.25, 17) * mm});
            skLineSegment(sketch, "E107", {"start": v(34.25, 17) * mm, "end": v(34.25, 5) * mm});
            skLineSegment(sketch, "E108", {"start": v(34.25, 5) * mm, "end": v(37.25, 5) * mm});
            skLineSegment(sketch, "E109", {"start": v(37.25, 5) * mm, "end": v(37.25, 17) * mm});
            skLineSegment(sketch, "E110", {"start": v(42.25, 17) * mm, "end": v(42.25, 5) * mm});
            skLineSegment(sketch, "E111", {"start": v(42.25, 5) * mm, "end": v(45.25, 5) * mm});
            skLineSegment(sketch, "E112", {"start": v(45.25, 5) * mm, "end": v(45.25, 17) * mm});
            skLineSegment(sketch, "E113", {"start": v(50.25, 17) * mm, "end": v(50.25, 5) * mm});
            skLineSegment(sketch, "E114", {"start": v(50.25, 5) * mm, "end": v(53.25, 5) * mm});
            skLineSegment(sketch, "E115", {"start": v(53.25, 5) * mm, "end": v(53.25, 17) * mm});
            skSolve(sketch);
        }
        {
            var Q0;
            {var subQ0=sQuery(id+"F8.wireOp",EDGE,"E96");Q0=makeQuery(id+"F8.imprint","IMPRINT",FACE,{"disambiguationData":[TD([[makeQuery(id+"F8.imprint","IMPRINT",EDGE,{"derivedFrom":subQ0}),1.0]])]});}
            var Q1;
            {var subQ0=sQuery(id+"F8.wireOp",EDGE,"E99");Q1=makeQuery(id+"F8.imprint","IMPRINT",FACE,{"disambiguationData":[TD([[makeQuery(id+"F8.imprint","IMPRINT",EDGE,{"derivedFrom":subQ0}),1.0]])]});}
            extrude(context, id + "F9", {"entities" : qUnion([Q0, Q1]), "operationType" : NewBodyOperationType.REMOVE, "oppositeDirection" : true, "depth" : 4 * mm});
        }
        {
            var Q0;
            Q0 = qSketchRegion(id + "F8", true);
            extrude(context, id + "F10", {"entities" : qUnion([Q0]), "operationType" : NewBodyOperationType.REMOVE, "oppositeDirection" : true, "depth" : 1 * mm});
        }
        {
            var Q0;
            {var subQ0=sQuery(id+"F4.wireOp",EDGE,"E71");Q0=makeQuery(id+"F4.imprint","IMPRINT",FACE,{"disambiguationData":[TD([[makeQuery(id+"F4.imprint","IMPRINT",EDGE,{"derivedFrom":subQ0}),1.0]])]});}
            var Q1;
            {var subQ0=sQuery(id+"F4.wireOp",EDGE,"E75");Q1=makeQuery(id+"F4.imprint","IMPRINT",FACE,{"disambiguationData":[TD([[makeQuery(id+"F4.imprint","IMPRINT",EDGE,{"derivedFrom":subQ0}),1.0]])]});}
            var Q2;
            {var subQ0=sQuery(id+"F4.wireOp",EDGE,"E79");Q2=makeQuery(id+"F4.imprint","IMPRINT",FACE,{"disambiguationData":[TD([[makeQuery(id+"F4.imprint","IMPRINT",EDGE,{"derivedFrom":subQ0}),1.0]])]});}
            var Q3;
            Q3=makeQuery(id+"F4.imprint","IMPRINT",FACE,{"disambiguationData":[TD([[makeQuery(id+"F4.imprint","IMPRINT",EDGE,{"derivedFrom":sQuery(id+"F4.wireOp",EDGE,"E82.MirrorCS")}),-1.0]])]});
            var Q4;
            Q4=makeQuery(id+"F4.imprint","IMPRINT",FACE,{"disambiguationData":[TD([[makeQuery(id+"F4.imprint","IMPRINT",EDGE,{"derivedFrom":sQuery(id+"F4.wireOp",EDGE,"E84.MirrorCS")}),-1.0]])]});
            var Q5;
            Q5=makeQuery(id+"F4.imprint","IMPRINT",FACE,{"disambiguationData":[TD([[makeQuery(id+"F4.imprint","IMPRINT",EDGE,{"derivedFrom":sQuery(id+"F4.wireOp",EDGE,"E86.MirrorCS")}),-1.0]])]});
            extrude(context, id + "F11", {"entities" : qUnion([Q0, Q1, Q2, Q3, Q4, Q5]), "operationType" : NewBodyOperationType.REMOVE, "oppositeDirection" : true, "depth" : 1 * mm});
        }
        {
            var Q0;
            {var subQ0=sQuery(id+"F0.wireOp",EDGE,"MmGPWXn9-bgj3-SnPU-f73x-K2FSZj5xh2pY");Q0=makeQuery(id+"F0.imprint","IMPRINT",FACE,{"disambiguationData":[TD([[makeQuery(id+"F0.imprint","IMPRINT",EDGE,{"derivedFrom":subQ0}),-1.0]])]});}
            var Q1;
            Q1=makeQuery(id+"F0.imprint","IMPRINT",FACE,{"disambiguationData":[TD([[makeQuery(id+"F0.imprint","IMPRINT",EDGE,{"derivedFrom":sQuery(id+"F0.wireOp",EDGE,"E46.0")}),-1.0]])]});
            extrude(context, id + "F12", {"entities" : qUnion([Q0, Q1]), "operationType" : NewBodyOperationType.ADD, "depth" : 8 * mm});
        }
        {
            var Q0;
            Q0=makeQuery(id+"F0.imprint","IMPRINT",FACE,{"disambiguationData":[TD([[makeQuery(id+"F0.imprint","IMPRINT",EDGE,{"derivedFrom":sQuery(id+"F0.wireOp",EDGE,"E28")}),1.0]])]});
            extrude(context, id + "F13", {"entities" : qUnion([Q0]), "operationType" : NewBodyOperationType.ADD, "depth" : 7 * mm});
        }
        {
            var Q0;
            {var subQ0=sQuery(id+"F0.wireOp",EDGE,"ythX9w36-mhEy-aItk-m4XK-AgucC76ztnV9");Q0=makeQuery(id+"F0.imprint","IMPRINT",FACE,{"disambiguationData":[TD([[makeQuery(id+"F0.imprint","IMPRINT",EDGE,{"derivedFrom":subQ0}),1.0]])]});}
            var Q1;
            {var subQ1=sQuery(id+"F0.wireOp",EDGE,"E16");Q1=makeQuery(id+"F0.imprint","IMPRINT",FACE,{"disambiguationData":[TD([[makeQuery(id+"F0.imprint","IMPRINT",EDGE,{"derivedFrom":subQ1}),-1.0]])]});}
            var Q2;
            Q2=makeQuery(id+"F0.imprint","IMPRINT",FACE,{"disambiguationData":[TD([[makeQuery(id+"F0.imprint","IMPRINT",EDGE,{"derivedFrom":sQuery(id+"F0.wireOp",EDGE,"E17")}),-1.0]])]});
            extrude(context, id + "F14", {"entities" : qUnion([Q0, Q1, Q2]), "operationType" : NewBodyOperationType.ADD, "depth" : 6 * mm});
        }
        {
            var Q0;
            Q0=makeQuery(id+"F12.opExtrude","SWEPT_FACE",FACE,{"disambiguationData":[OSD([sQuery(id+"F0.wireOp",EDGE,"E47"),sQuery(id+"F0.wireOp",EDGE,"E50")])]});
            var sketch = newSketch(context, id + "F15", { "sketchPlane" : qUnion([Q0])});
            skLineSegment(sketch, "E116", {"start": v(53.25, 8) * mm, "end": v(56.25, 8) * mm});
            skLineSegment(sketch, "E117", {"start": v(56.25, 8) * mm, "end": v(56.25, 5) * mm});
            skCircle(sketch, "E118", {"center": v(56.25, 5) * mm, "radius": 2 * mm});
            skSolve(sketch);
        }
        {
            var Q0;
            Q0 = qSketchRegion(id + "F15", true);
            extrude(context, id + "F16", {"entities" : qUnion([Q0]), "operationType" : NewBodyOperationType.REMOVE, "oppositeDirection" : true, "depth" : 3 * mm});
        }
    });
